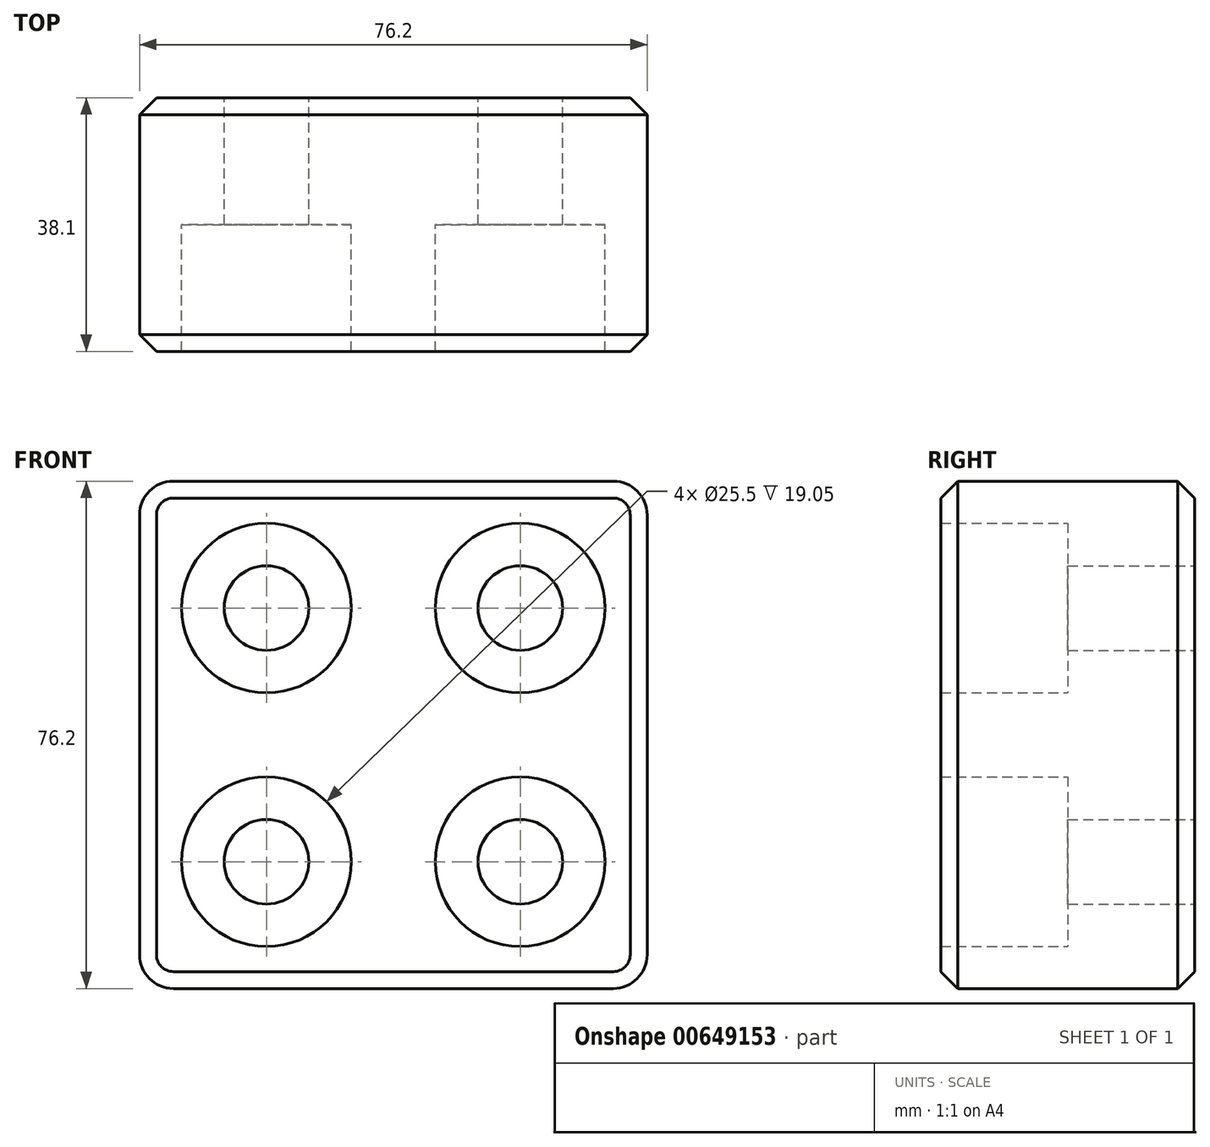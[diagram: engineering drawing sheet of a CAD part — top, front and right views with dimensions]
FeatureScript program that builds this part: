
annotation { "Feature Type Name" : "Feature", "Feature Type Description" : "" }
export const myFeature = defineFeature(function(context is Context, id is Id, definition is map)
    precondition{}
    {
        {
            var Q0;
            Q0=qCreatedBy(makeId("Front.planeOp"),FACE);
            var sketch = newSketch(context, id + "F0", { "sketchPlane" : qUnion([Q0])});
            skLineSegment(sketch, "E0.bottom", {"start": v(-38.1, 38.1) * mm, "end": v(38.1, 38.1) * mm});
            skLineSegment(sketch, "E0.top", {"start": v(-38.1, -38.1) * mm, "end": v(38.1, -38.1) * mm});
            skLineSegment(sketch, "E0.left", {"start": v(-38.1, 38.1) * mm, "end": v(-38.1, -38.1) * mm});
            skLineSegment(sketch, "E0.right", {"start": v(38.1, 38.1) * mm, "end": v(38.1, -38.1) * mm});
            skLineSegment(sketch, "E1", {"start": v(0, 0) * mm, "end": v(0, 38.1) * mm, "construction": true});
            skLineSegment(sketch, "E2", {"start": v(0, 0) * mm, "end": v(38.1, 0) * mm, "construction": true});
            skCircle(sketch, "E3", {"center": v(-19.05, 19.05) * mm, "radius": 6.35 * mm});
            skCircle(sketch, "E4", {"center": v(19.05, 19.05) * mm, "radius": 6.35 * mm});
            skCircle(sketch, "E5", {"center": v(19.05, -19.05) * mm, "radius": 6.35 * mm});
            skCircle(sketch, "E6", {"center": v(-19.05, -19.05) * mm, "radius": 6.35 * mm});
            skSolve(sketch);
        }
        {
            var Q0;
            Q0=makeQuery(id+"F0.imprint","IMPRINT",FACE,{"disambiguationData":[TD([[makeQuery(id+"F0.imprint","IMPRINT",EDGE,{"derivedFrom":sQuery(id+"F0.wireOp",EDGE,"E0.bottom")}),-1.0]])]});
            extrude(context, id + "F1", {"entities" : qUnion([Q0]), "endBound" : BoundingType.SYMMETRIC, "depth" : 38.1 * mm, "offsetDistance" : 25.4 * mm});
        }
        {
            var Q0;
            Q0=makeQuery(id+"F1.opExtrude","SWEPT_EDGE",EDGE,{"disambiguationData":[OSD([sQuery(id+"F0.wireOp",EDGE,"E0.bottom"),sQuery(id+"F0.wireOp",EDGE,"E0.right")])]});
            var Q1;
            Q1=makeQuery(id+"F1.opExtrude","SWEPT_EDGE",EDGE,{"disambiguationData":[OSD([sQuery(id+"F0.wireOp",EDGE,"E0.bottom"),sQuery(id+"F0.wireOp",EDGE,"E0.left")])]});
            var Q2;
            Q2=makeQuery(id+"F1.opExtrude","SWEPT_EDGE",EDGE,{"disambiguationData":[OSD([sQuery(id+"F0.wireOp",EDGE,"E0.top"),sQuery(id+"F0.wireOp",EDGE,"E0.left")])]});
            var Q3;
            Q3=makeQuery(id+"F1.opExtrude","SWEPT_EDGE",EDGE,{"disambiguationData":[OSD([sQuery(id+"F0.wireOp",EDGE,"E0.top"),sQuery(id+"F0.wireOp",EDGE,"E0.right")])]});
            fillet(context, id + "F2", {"entities" : qUnion([Q0, Q1, Q2, Q3]), "radius" : 5.08 * mm, "tangentPropagation" : true, "allowEdgeOverflow" : false});
        }
        {
            var Q0;
            Q0=sQuery(id+"F0.wireOp",VERTEX,"E3.center");
            var Q1;
            Q1=sQuery(id+"F0.wireOp",VERTEX,"E6.center");
            var Q2;
            Q2=sQuery(id+"F0.wireOp",VERTEX,"E5.center");
            var Q3;
            Q3=sQuery(id+"F0.wireOp",VERTEX,"E4.center");
            var Q4;
            Q4=makeQuery(id+"F1.opExtrude","SWEPT_BODY",BODY,{"disambiguationData":[OSD([sQuery(id+"F0.wireOp",EDGE,"E0.bottom"),sQuery(id+"F0.wireOp",EDGE,"E0.top"),sQuery(id+"F0.wireOp",EDGE,"E0.left"),sQuery(id+"F0.wireOp",EDGE,"E0.right"),sQuery(id+"F0.wireOp",EDGE,"E3"),sQuery(id+"F0.wireOp",EDGE,"E4"),sQuery(id+"F0.wireOp",EDGE,"E5"),sQuery(id+"F0.wireOp",EDGE,"E6")])]});
            hole(context, id + "F3", {"style" : HoleStyle.C_BORE, "endStyle" : HoleEndStyle.THROUGH, "oppositeDirection" : true, "holeDiameter" : 17.5 * mm, "cBoreDiameter" : 25.5 * mm, "cBoreDepth" : 30 * mm, "majorDiameter" : 6.35 * mm, "isTappedThrough" : true, "tappedDepth" : 12.7 * mm, "tapClearance" : 3, "startFromSketch" : true, "locations" : qUnion([Q0, Q1, Q2, Q3]), "scope" : qUnion([Q4])});
        }
        {
            var Q0;
            Q0=makeQuery(id+"F1.opExtrude","CAP_EDGE",EDGE,{"disambiguationData":[OSD([sQuery(id+"F0.wireOp",EDGE,"E0.top")])],"isStart":true});
            var Q1;
            Q1=makeQuery(id+"F3.hole-2.boolean.opBoolean","INTERSECT",EDGE,{"derivedFrom":[makeQuery(id+"F1.opExtrude","CAP_FACE",FACE,{"disambiguationData":[OSD([sQuery(id+"F0.wireOp",EDGE,"E0.bottom"),sQuery(id+"F0.wireOp",EDGE,"E0.top"),sQuery(id+"F0.wireOp",EDGE,"E0.left"),sQuery(id+"F0.wireOp",EDGE,"E0.right"),sQuery(id+"F0.wireOp",EDGE,"E3"),sQuery(id+"F0.wireOp",EDGE,"E4"),sQuery(id+"F0.wireOp",EDGE,"E5"),sQuery(id+"F0.wireOp",EDGE,"E6")])],"isStart":false}),makeQuery(id+"F3.hole-2.opRevolve","SWEPT_FACE",FACE,{"disambiguationData":[OSD([sQuery(id+"F3.hole-2.sketch.wireOp",EDGE,"cbore_start_line_2")])]})]});
            var Q2;
            Q2=makeQuery(id+"F3.hole-3.boolean.opBoolean","INTERSECT",EDGE,{"derivedFrom":[makeQuery(id+"F1.opExtrude","CAP_FACE",FACE,{"disambiguationData":[OSD([sQuery(id+"F0.wireOp",EDGE,"E0.bottom"),sQuery(id+"F0.wireOp",EDGE,"E0.top"),sQuery(id+"F0.wireOp",EDGE,"E0.left"),sQuery(id+"F0.wireOp",EDGE,"E0.right"),sQuery(id+"F0.wireOp",EDGE,"E3"),sQuery(id+"F0.wireOp",EDGE,"E4"),sQuery(id+"F0.wireOp",EDGE,"E5"),sQuery(id+"F0.wireOp",EDGE,"E6")])],"isStart":false}),makeQuery(id+"F3.hole-3.opRevolve","SWEPT_FACE",FACE,{"disambiguationData":[OSD([sQuery(id+"F3.hole-3.sketch.wireOp",EDGE,"cbore_start_line_2")])]})]});
            var Q3;
            Q3=makeQuery(id+"F3.hole-0.boolean.opBoolean","INTERSECT",EDGE,{"derivedFrom":[makeQuery(id+"F1.opExtrude","CAP_FACE",FACE,{"disambiguationData":[OSD([sQuery(id+"F0.wireOp",EDGE,"E0.bottom"),sQuery(id+"F0.wireOp",EDGE,"E0.top"),sQuery(id+"F0.wireOp",EDGE,"E0.left"),sQuery(id+"F0.wireOp",EDGE,"E0.right"),sQuery(id+"F0.wireOp",EDGE,"E3"),sQuery(id+"F0.wireOp",EDGE,"E4"),sQuery(id+"F0.wireOp",EDGE,"E5"),sQuery(id+"F0.wireOp",EDGE,"E6")])],"isStart":false}),makeQuery(id+"F3.hole-0.opRevolve","SWEPT_FACE",FACE,{"disambiguationData":[OSD([sQuery(id+"F3.hole-0.sketch.wireOp",EDGE,"cbore_start_line_2")])]})]});
            var Q4;
            Q4=makeQuery(id+"F3.hole-1.boolean.opBoolean","INTERSECT",EDGE,{"derivedFrom":[makeQuery(id+"F1.opExtrude","CAP_FACE",FACE,{"disambiguationData":[OSD([sQuery(id+"F0.wireOp",EDGE,"E0.bottom"),sQuery(id+"F0.wireOp",EDGE,"E0.top"),sQuery(id+"F0.wireOp",EDGE,"E0.left"),sQuery(id+"F0.wireOp",EDGE,"E0.right"),sQuery(id+"F0.wireOp",EDGE,"E3"),sQuery(id+"F0.wireOp",EDGE,"E4"),sQuery(id+"F0.wireOp",EDGE,"E5"),sQuery(id+"F0.wireOp",EDGE,"E6")])],"isStart":false}),makeQuery(id+"F3.hole-1.opRevolve","SWEPT_FACE",FACE,{"disambiguationData":[OSD([sQuery(id+"F3.hole-1.sketch.wireOp",EDGE,"cbore_start_line_2")])]})]});
            var Q5;
            Q5=makeQuery(id+"F1.opExtrude","CAP_EDGE",EDGE,{"disambiguationData":[OSD([sQuery(id+"F0.wireOp",EDGE,"E0.top")])],"isStart":false});
            chamfer(context, id + "F4", {"entities" : qUnion([Q0, Q1, Q2, Q3, Q4, Q5]), "width" : 2.54 * mm, "tangentPropagation" : true});
        }
    });
